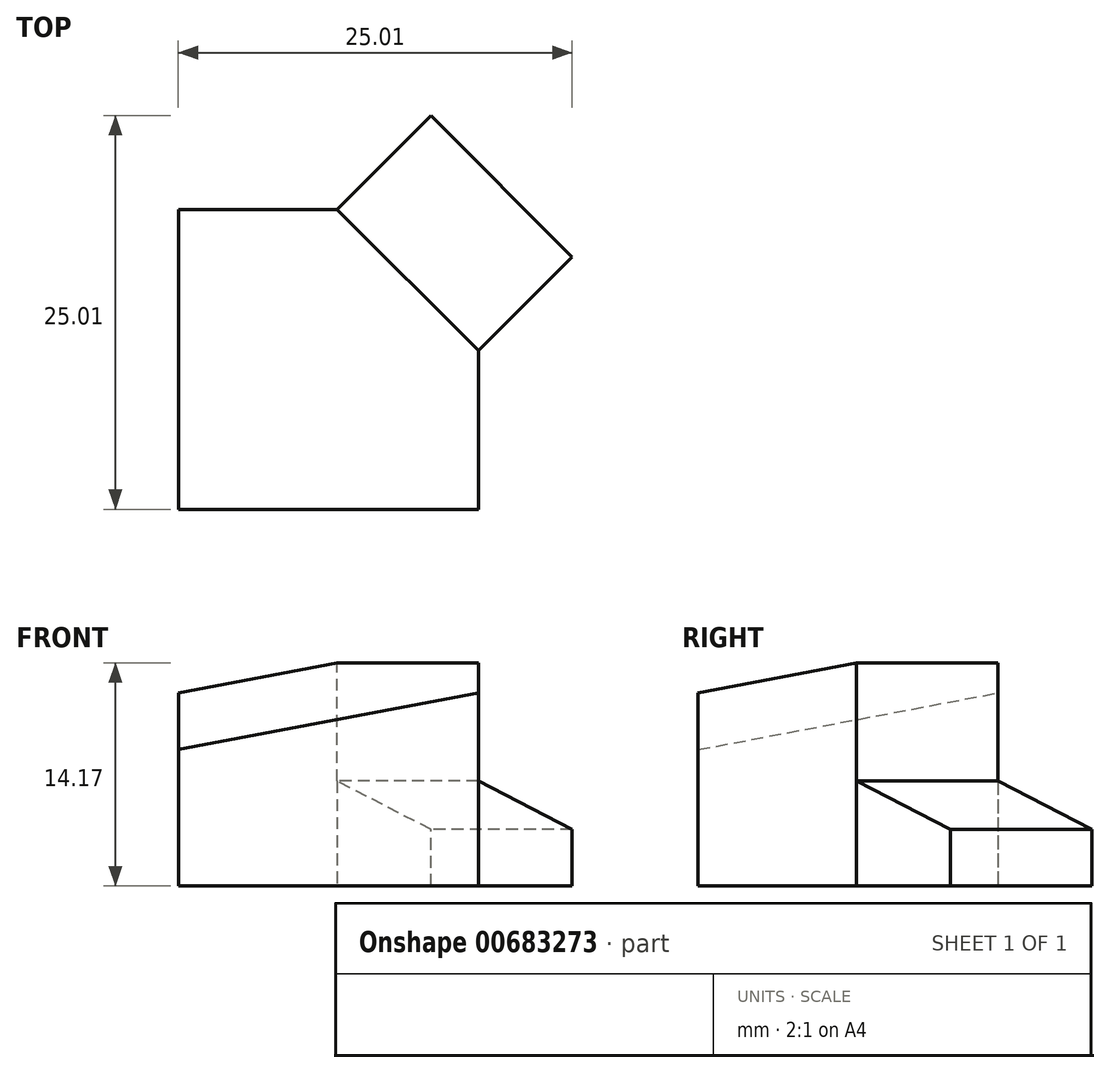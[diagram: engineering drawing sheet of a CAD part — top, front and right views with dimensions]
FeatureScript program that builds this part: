
annotation { "Feature Type Name" : "Feature", "Feature Type Description" : "" }
export const myFeature = defineFeature(function(context is Context, id is Id, definition is map)
    precondition{}
    {
        {
            var Q0;
            Q0=qCreatedBy(makeId("Top.planeOp"),FACE);
            var sketch = newSketch(context, id + "F0", { "sketchPlane" : qUnion([Q0])});
            skLineSegment(sketch, "E0.bottom", {"start": v(-9.52, 9.52) * mm, "end": v(9.53, 9.52) * mm});
            skLineSegment(sketch, "E0.top", {"start": v(-9.53, -9.52) * mm, "end": v(9.53, -9.52) * mm});
            skLineSegment(sketch, "E0.left", {"start": v(-9.52, 9.52) * mm, "end": v(-9.53, -9.52) * mm});
            skLineSegment(sketch, "E0.right", {"start": v(9.53, 9.52) * mm, "end": v(9.53, -9.52) * mm});
            skPoint(sketch, "E0.middle", {"position": v(0, 0) * mm});
            skSolve(sketch);
        }
        {
            var Q0;
            Q0 = qSketchRegion(id + "F0", true);
            extrude(context, id + "F1", {"entities" : qUnion([Q0]), "depth" : 15.88 * mm, "offsetDistance" : 25.4 * mm});
        }
        {
            var Q0;
            Q0=makeQuery(id+"F1.opExtrude","SWEPT_EDGE",EDGE,{"disambiguationData":[OSD([sQuery(id+"F0.wireOp",EDGE,"E0.top"),sQuery(id+"F0.wireOp",EDGE,"E0.left")])]});
            cPlane(context, id + "F2", {"entities" : qUnion([Q0]), "cplaneType" : CPlaneType.LINE_ANGLE, "offset" : 0 * mm, "angle" : 135 * degree, "oppositeDirection" : true, "width" : 152.4 * mm, "height" : 152.4 * mm});
        }
        {
            var Q0;
            Q0=qCreatedBy(id+"F2.planeOp",FACE);
            var sketch = newSketch(context, id + "F3", { "sketchPlane" : qUnion([Q0])});
            skLineSegment(sketch, "E1", {"start": v(13.47, 15.88) * mm, "end": v(-20.73, 6.71) * mm});
            skLineSegment(sketch, "E2", {"start": v(-20.73, 6.71) * mm, "end": v(-26.84, 15.88) * mm});
            skLineSegment(sketch, "E3", {"start": v(-26.84, 15.88) * mm, "end": v(13.47, 15.88) * mm});
            skPoint(sketch, "E4.orphan", {"position": v(-13.47, 15.88) * mm});
            skPoint(sketch, "E5.0.end.orphan", {"position": v(-13.47, 0) * mm});
            skPoint(sketch, "E6.start.orphan", {"position": v(0, 26.18) * mm});
            skSolve(sketch);
        }
        {
            var Q0;
            Q0 = qSketchRegion(id + "F3", true);
            extrude(context, id + "F4", {"entities" : qUnion([Q0]), "operationType" : NewBodyOperationType.REMOVE, "endBound" : BoundingType.SYMMETRIC, "depth" : 37.6 * mm, "offsetDistance" : 25.4 * mm});
        }
        {
            var Q0;
            Q0=qCreatedBy(id+"F2.planeOp",FACE);
            var sketch = newSketch(context, id + "F5", { "sketchPlane" : qUnion([Q0])});
            skLineSegment(sketch, "E7", {"start": v(13.47, 0) * mm, "end": v(25.41, 0) * mm});
            skLineSegment(sketch, "E8", {"start": v(25.41, 0) * mm, "end": v(5.38, 7.3) * mm});
            skLineSegment(sketch, "E9", {"start": v(13.47, 0) * mm, "end": v(5.32, 0) * mm});
            skLineSegment(sketch, "E10", {"start": v(5.32, 0) * mm, "end": v(5.38, 7.3) * mm});
            skPoint(sketch, "E11.0.start.orphan", {"position": v(13.47, 15.88) * mm});
            skSolve(sketch);
        }
        {
            var Q0;
            Q0 = qSketchRegion(id + "F5", true);
            extrude(context, id + "F6", {"entities" : qUnion([Q0]), "operationType" : NewBodyOperationType.ADD, "endBound" : BoundingType.SYMMETRIC, "depth" : 12.7 * mm, "offsetDistance" : 25.4 * mm});
        }
        {
            var Q0;
            Q0=qCreatedBy(id+"F2.planeOp",FACE);
            var sketch = newSketch(context, id + "F7", { "sketchPlane" : qUnion([Q0])});
            skLineSegment(sketch, "E12", {"start": v(7.12, 6.66) * mm, "end": v(7.12, 16.24) * mm});
            skLineSegment(sketch, "E13", {"start": v(7.12, 16.24) * mm, "end": v(14.02, 17.52) * mm});
            skLineSegment(sketch, "E14", {"start": v(15.55, 3.6) * mm, "end": v(15.55, 0) * mm});
            skPoint(sketch, "E15.0.start.orphan", {"position": v(25.41, 0) * mm});
            skLineSegment(sketch, "E16", {"start": v(7.12, 6.66) * mm, "end": v(15.55, 3.6) * mm});
            skPoint(sketch, "E17.end.orphan", {"position": v(7.12, 0) * mm});
            skLineSegment(sketch, "E18", {"start": v(15.55, 0) * mm, "end": v(25.41, 0) * mm});
            skLineSegment(sketch, "E19", {"start": v(25.41, 0) * mm, "end": v(14.02, 17.52) * mm});
            skSolve(sketch);
        }
        {
            var Q0;
            Q0 = qSketchRegion(id + "F7", true);
            extrude(context, id + "F8", {"entities" : qUnion([Q0]), "operationType" : NewBodyOperationType.REMOVE, "endBound" : BoundingType.SYMMETRIC, "depth" : 25.4 * mm, "offsetDistance" : 25.4 * mm});
        }
    });
